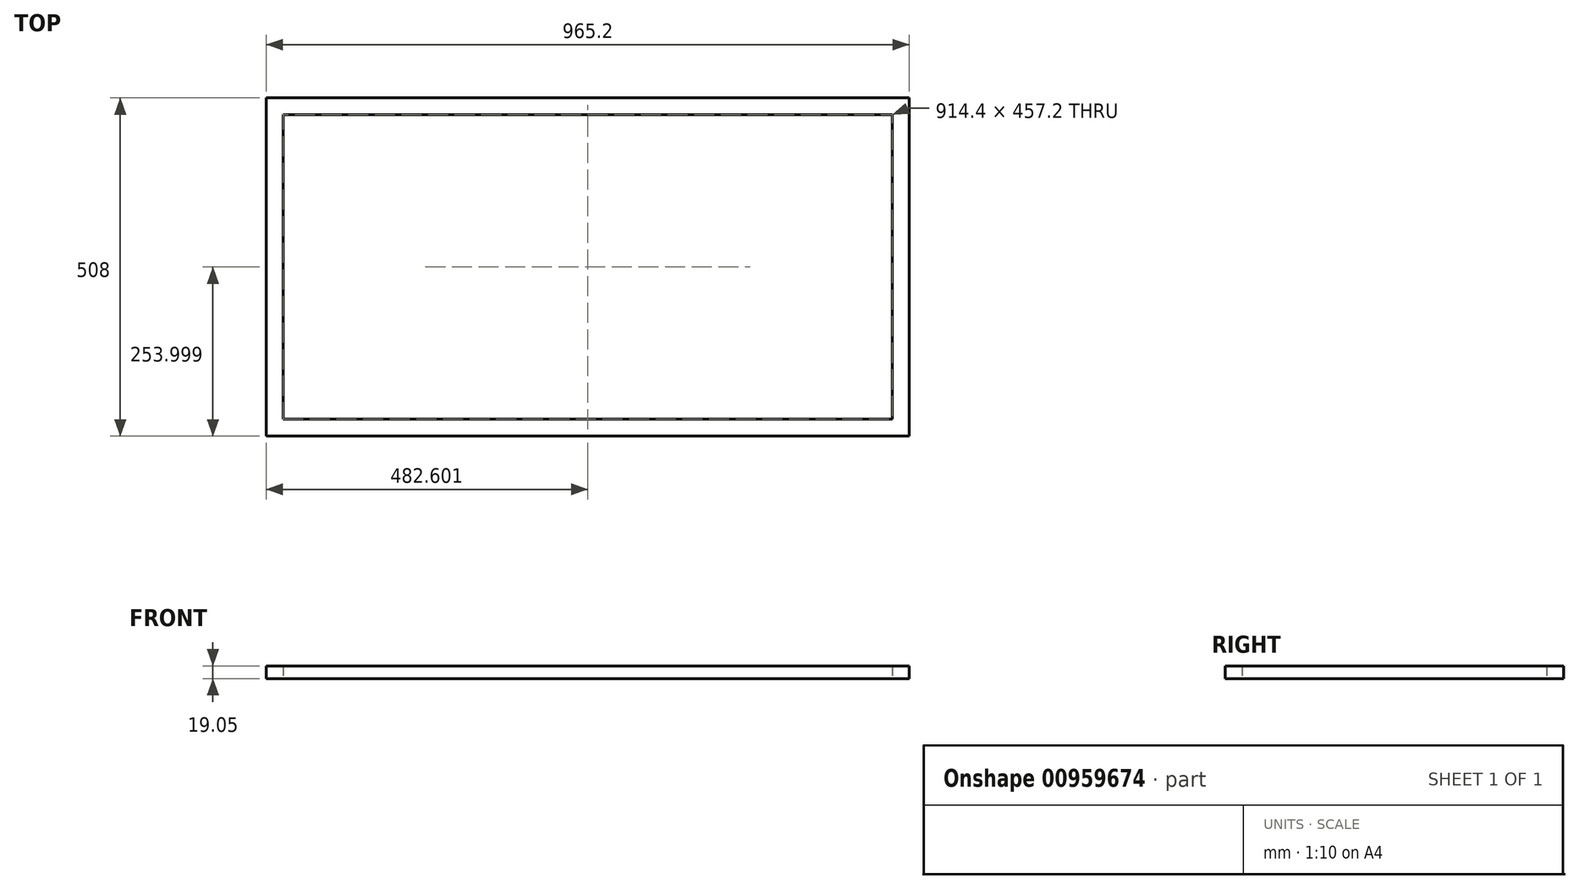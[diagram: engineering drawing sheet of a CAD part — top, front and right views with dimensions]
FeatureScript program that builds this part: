
annotation { "Feature Type Name" : "Feature", "Feature Type Description" : "" }
export const myFeature = defineFeature(function(context is Context, id is Id, definition is map)
    precondition{}
    {
        {
            var Q0;
            Q0=qCreatedBy(makeId("Top.planeOp"),FACE);
            var sketch = newSketch(context, id + "F0", { "sketchPlane" : qUnion([Q0])});
            skLineSegment(sketch, "E0.bottom", {"start": v(-879.33, 269.99) * mm, "end": v(85.87, 269.99) * mm});
            skLineSegment(sketch, "E0.top", {"start": v(-879.33, -238.01) * mm, "end": v(85.87, -238.01) * mm});
            skLineSegment(sketch, "E0.left", {"start": v(-879.33, 269.99) * mm, "end": v(-879.33, -238.01) * mm});
            skLineSegment(sketch, "E0.right", {"start": v(85.87, 269.99) * mm, "end": v(85.87, -238.01) * mm});
            skLineSegment(sketch, "E1.bottom", {"start": v(-853.93, 244.59) * mm, "end": v(60.47, 244.59) * mm});
            skLineSegment(sketch, "E1.top", {"start": v(-853.93, -212.61) * mm, "end": v(60.47, -212.61) * mm});
            skLineSegment(sketch, "E1.left", {"start": v(-853.93, 244.59) * mm, "end": v(-853.93, -212.61) * mm});
            skLineSegment(sketch, "E1.right", {"start": v(60.47, 244.59) * mm, "end": v(60.47, -212.61) * mm});
            skSolve(sketch);
        }
        {
            var Q0;
            Q0=makeQuery(id+"F0.imprint","IMPRINT",FACE,{"disambiguationData":[TD([[makeQuery(id+"F0.imprint","IMPRINT",EDGE,{"derivedFrom":sQuery(id+"F0.wireOp",EDGE,"E0.bottom")}),-1.0]])]});
            extrude(context, id + "F1", {"entities" : qUnion([Q0]), "depth" : 19.05 * mm, "offsetDistance" : 25.4 * mm});
        }
    });
